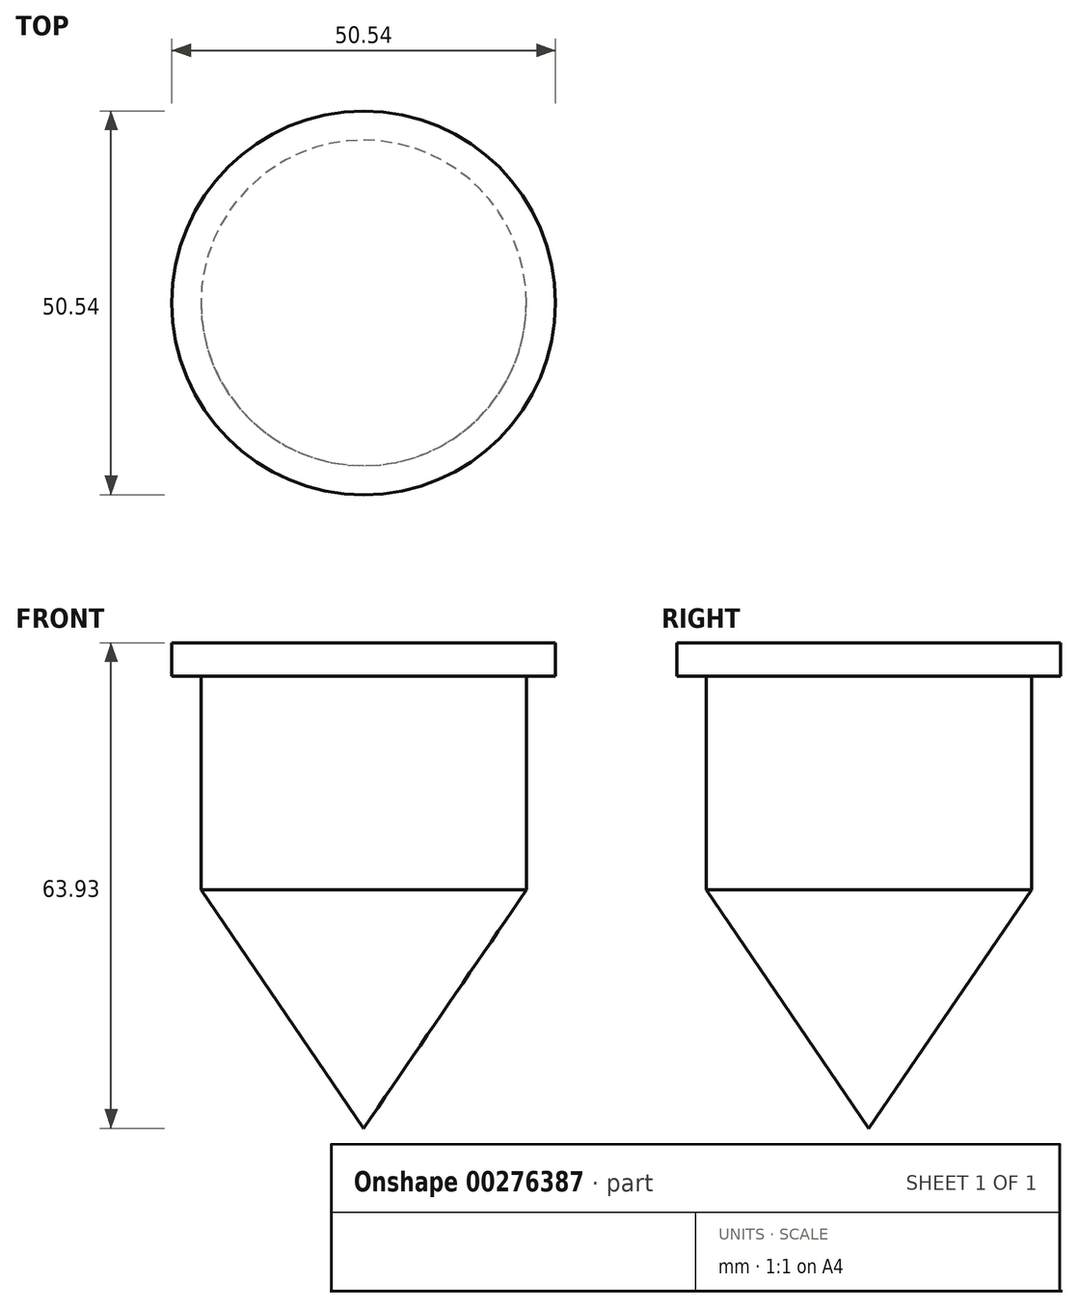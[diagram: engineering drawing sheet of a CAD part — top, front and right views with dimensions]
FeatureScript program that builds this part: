
annotation { "Feature Type Name" : "Feature", "Feature Type Description" : "" }
export const myFeature = defineFeature(function(context is Context, id is Id, definition is map)
    precondition{}
    {
        {
            var Q0;
            Q0=qCreatedBy(makeId("Front.planeOp"),FACE);
            var sketch = newSketch(context, id + "F0", { "sketchPlane" : qUnion([Q0])});
            skLineSegment(sketch, "E0", {"start": v(-16.27, 37.9) * mm, "end": v(-41.54, 37.9) * mm});
            skLineSegment(sketch, "E1", {"start": v(-41.54, 37.9) * mm, "end": v(-41.54, 33.5) * mm});
            skLineSegment(sketch, "E2", {"start": v(-41.54, 33.5) * mm, "end": v(-37.7, 33.5) * mm});
            skLineSegment(sketch, "E3", {"start": v(-37.7, 33.5) * mm, "end": v(-37.7, 5.36) * mm});
            skLineSegment(sketch, "E4", {"start": v(-37.7, 5.36) * mm, "end": v(-16.27, -26.03) * mm});
            skLineSegment(sketch, "E5", {"start": v(-16.27, -26.03) * mm, "end": v(-16.27, 37.9) * mm});
            skSolve(sketch);
        }
        {
            var Q0;
            Q0=makeQuery(id+"F0.imprint","IMPRINT",FACE,{"disambiguationData":[TD([[makeQuery(id+"F0.imprint","IMPRINT",EDGE,{"derivedFrom":sQuery(id+"F0.wireOp",EDGE,"E0")}),1.0]])]});
            var Q1;
            Q1=sQuery(id+"F0.wireOp",EDGE,"E5");
            revolve(context, id + "F1", {"entities" : qUnion([Q0]), "axis" : qUnion([Q1]), "revolveType" : RevolveType.FULL});
        }
    });
